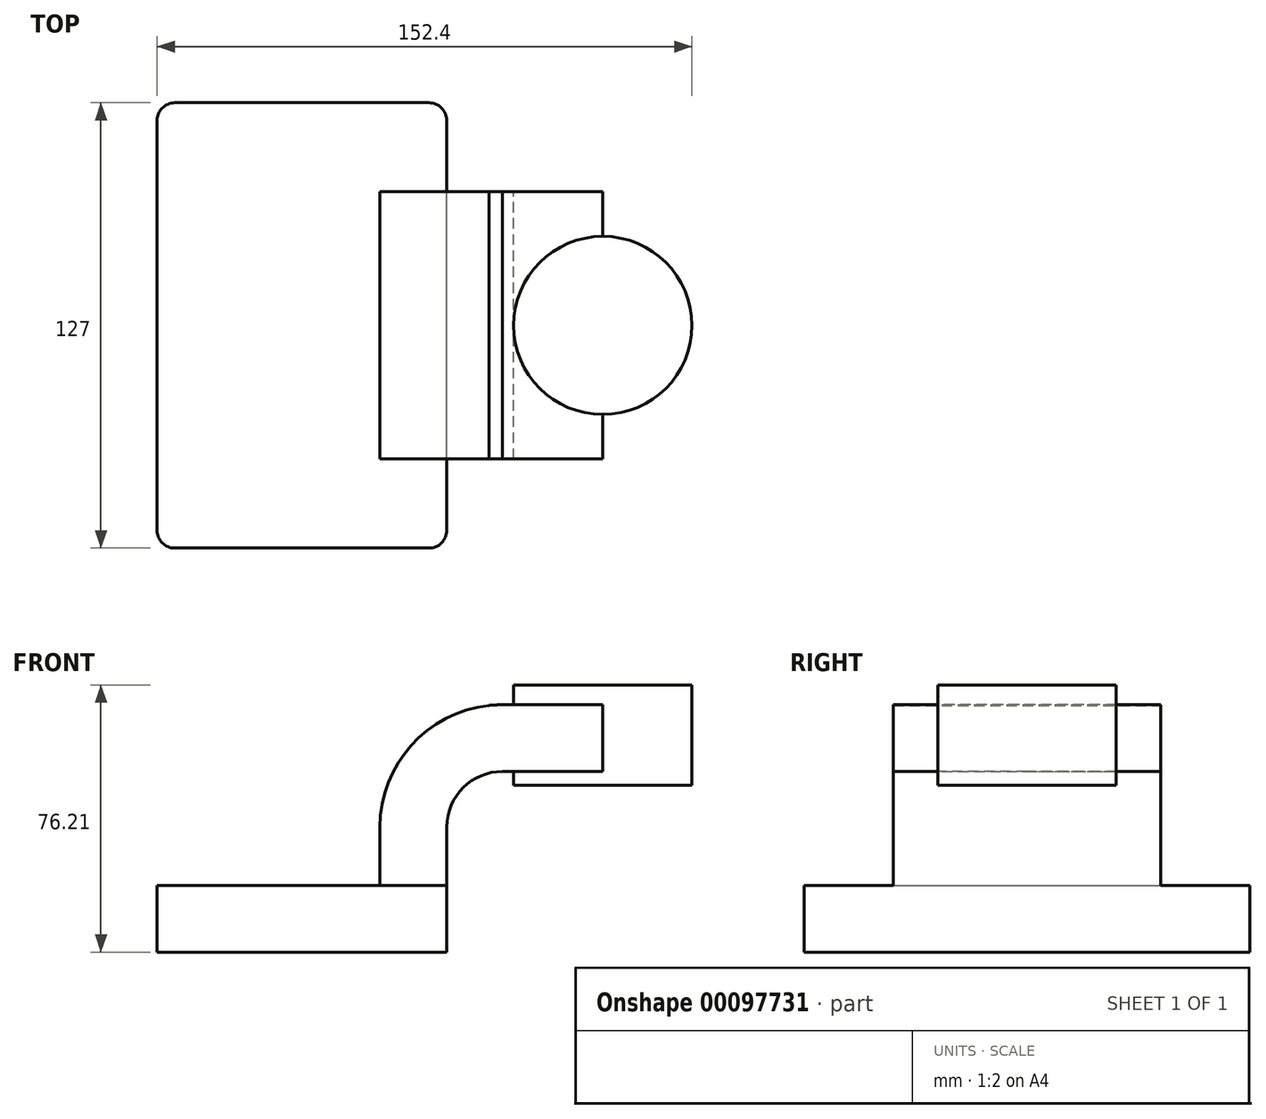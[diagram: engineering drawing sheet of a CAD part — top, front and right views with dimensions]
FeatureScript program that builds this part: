
annotation { "Feature Type Name" : "Feature", "Feature Type Description" : "" }
export const myFeature = defineFeature(function(context is Context, id is Id, definition is map)
    precondition{}
    {
        {
            var Q0;
            Q0=qCreatedBy(makeId("Front.planeOp"),FACE);
            var sketch = newSketch(context, id + "F0", { "sketchPlane" : qUnion([Q0])});
            skLineSegment(sketch, "E0.bottom", {"start": v(41.28, -9.52) * mm, "end": v(-41.28, -9.53) * mm});
            skLineSegment(sketch, "E0.top", {"start": v(41.28, 9.53) * mm, "end": v(-41.28, 9.52) * mm});
            skLineSegment(sketch, "E0.left", {"start": v(41.28, -9.53) * mm, "end": v(41.28, 9.53) * mm});
            skLineSegment(sketch, "E0.right", {"start": v(-41.28, -9.53) * mm, "end": v(-41.28, 9.52) * mm});
            skPoint(sketch, "E0.middle", {"position": v(0, 0) * mm});
            skLineSegment(sketch, "E1.bottom", {"start": v(60.32, 38.1) * mm, "end": v(111.12, 38.1) * mm});
            skLineSegment(sketch, "E1.top", {"start": v(60.32, 66.68) * mm, "end": v(111.12, 66.68) * mm});
            skLineSegment(sketch, "E1.left", {"start": v(60.32, 38.1) * mm, "end": v(60.32, 66.67) * mm});
            skLineSegment(sketch, "E1.right", {"start": v(111.12, 38.1) * mm, "end": v(111.12, 66.67) * mm});
            skPoint(sketch, "E1.middle", {"position": v(85.72, 52.39) * mm});
            skLineSegment(sketch, "E2", {"start": v(41.28, 9.53) * mm, "end": v(41.28, 26.12) * mm});
            skArc(sketch, "E3", {"start": v(41.28, 26.12) * mm, "mid": v(45.92, 37.34) * mm, "end": v(57.15, 42) * mm});
            skLineSegment(sketch, "E4", {"start": v(57.15, 42) * mm, "end": v(74.25, 42) * mm});
            skLineSegment(sketch, "E5.0", {"start": v(57.15, 61.04) * mm, "end": v(85.72, 61.04) * mm});
            skArc(sketch, "E5.1", {"start": v(22.23, 26.12) * mm, "mid": v(32.45, 50.81) * mm, "end": v(57.15, 61.04) * mm});
            skLineSegment(sketch, "E5.2", {"start": v(22.23, 9.53) * mm, "end": v(22.23, 26.12) * mm});
            skLineSegment(sketch, "E6.0", {"start": v(57.15, 41.99) * mm, "end": v(85.72, 41.99) * mm});
            skPoint(sketch, "E7.endSnap0", {"position": v(85.72, 66.68) * mm});
            skFitSpline(sketch, "E8", {"points": [v(-41.28, 9.52) * mm, v(57.15, 61.04) * mm], "startDerivative": vector(30.81, 96.21) * mm, "endDerivative": vector(163.23, 8) * mm});
            skLineSegment(sketch, "E9", {"start": v(85.72, 61.04) * mm, "end": v(85.72, 52.39) * mm});
            skLineSegment(sketch, "E10", {"start": v(85.72, 51.97) * mm, "end": v(85.72, 41.99) * mm});
            skLineSegment(sketch, "E11", {"start": v(85.72, 42.3) * mm, "end": v(85.72, 38.1) * mm});
            skLineSegment(sketch, "E12", {"start": v(85.72, 61.04) * mm, "end": v(85.72, 66.68) * mm});
            skLineSegment(sketch, "E13", {"start": v(85.72, 61.04) * mm, "end": v(85.72, 42.3) * mm});
            skSolve(sketch);
        }
        {
            var Q0;
            Q0=makeQuery(id+"F0.imprint","IMPRINT",FACE,{"disambiguationData":[TD([[makeQuery(id+"F0.imprint","IMPRINT",EDGE,{"derivedFrom":sQuery(id+"F0.wireOp",EDGE,"E0.bottom")}),-1.0]])]});
            extrude(context, id + "F1", {"entities" : qUnion([Q0]), "endBound" : BoundingType.SYMMETRIC, "depth" : 127 * mm});
        }
        {
            var Q0;
            {var subQ1=sQuery(id+"F0.wireOp",EDGE,"E2");Q0=makeQuery(id+"F0.imprint","IMPRINT",FACE,{"disambiguationData":[TD([[makeQuery(id+"F0.imprint","IMPRINT",EDGE,{"derivedFrom":subQ1}),1.0]])]});}
            var Q1;
            {var subQ5=sQuery(id+"F0.wireOp",EDGE,"E13");var subQ6=makeQuery(id+"F0.imprint","IMPRINT",VERTEX,{"disambiguationData":[OD(0.0)],"derivedFrom":subQ5});Q1=makeQuery(id+"F0.imprint","IMPRINT",FACE,{"disambiguationData":[TD([[makeQuery(id+"F0.imprint","IMPRINT",EDGE,{"disambiguationData":[TD([[subQ6,-1.0]])],"derivedFrom":subQ5}),-1.0]])]});}
            extrude(context, id + "F2", {"entities" : qUnion([Q0, Q1]), "operationType" : NewBodyOperationType.ADD, "endBound" : BoundingType.SYMMETRIC, "depth" : 76.2 * mm});
        }
        {
            var Q0;
            {var subQ0=sQuery(id+"F0.wireOp",EDGE,"E1.right");Q0=makeQuery(id+"F0.imprint","IMPRINT",FACE,{"disambiguationData":[TD([[makeQuery(id+"F0.imprint","IMPRINT",EDGE,{"derivedFrom":subQ0}),1.0]])]});}
            var Q1;
            Q1=sQuery(id+"F0.wireOp",EDGE,"E9");
            revolve(context, id + "F3", {"operationType" : NewBodyOperationType.ADD, "entities" : qUnion([Q0]), "axis" : qUnion([Q1]), "revolveType" : RevolveType.FULL});
        }
        {
            var Q0;
            Q0=makeQuery(id+"F1.opExtrude","CAP_EDGE",EDGE,{"disambiguationData":[OSD([sQuery(id+"F0.wireOp",EDGE,"E0.left")])],"isStart":false});
            fillet(context, id + "F4", {"entities" : qUnion([Q0]), "radius" : 5.08 * mm, "tangentPropagation" : true, "allowEdgeOverflow" : false});
        }
        {
            var Q0;
            Q0=makeQuery(id+"F1.opExtrude","CAP_EDGE",EDGE,{"disambiguationData":[OSD([sQuery(id+"F0.wireOp",EDGE,"E0.right")])],"isStart":true});
            var Q1;
            Q1=makeQuery(id+"F1.opExtrude","CAP_EDGE",EDGE,{"disambiguationData":[OSD([sQuery(id+"F0.wireOp",EDGE,"E0.right")])],"isStart":false});
            var Q2;
            Q2=makeQuery(id+"F1.opExtrude","CAP_EDGE",EDGE,{"disambiguationData":[OSD([sQuery(id+"F0.wireOp",EDGE,"E0.left")])],"isStart":true});
            fillet(context, id + "F5", {"entities" : qUnion([Q0, Q1, Q2]), "radius" : 5.08 * mm, "tangentPropagation" : true, "allowEdgeOverflow" : false});
        }
    });
